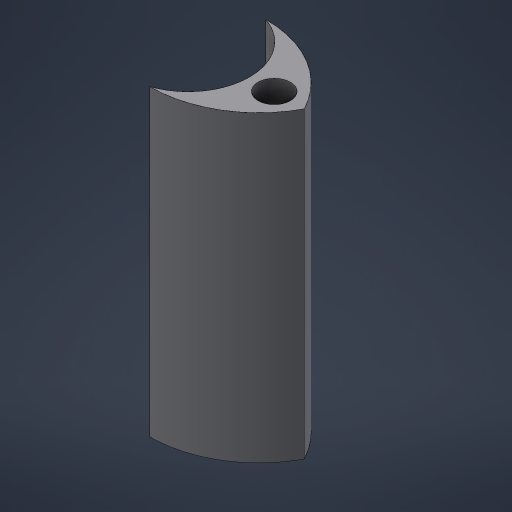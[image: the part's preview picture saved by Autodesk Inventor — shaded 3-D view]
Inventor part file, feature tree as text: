
AUTODESK INVENTOR PART (.ipt)
format: ipt  version: 2023.5 (Build 275446000, 446)  size: 210,944 bytes
history: native  units: mm
features: extrude x1, sketch x1
ambient origin geometry x8: Origin, YZ Plane, XZ Plane, XY Plane, X Axis, Y Axis, Z Axis, Center Point
bodies: Volumenkörper1 (feature_tree)
feature tree (2):
  extrude  "Extrusion1"  [1 undecoded]
  sketch  "Skizze1"  dims[d0=47.0mm d1=0.0mm]
note: 1 required parameter value undecoded (feature->parameter linkage not recoverable at this tier; creation-order binding heuristic only, values carry confidence <= 0.55)
